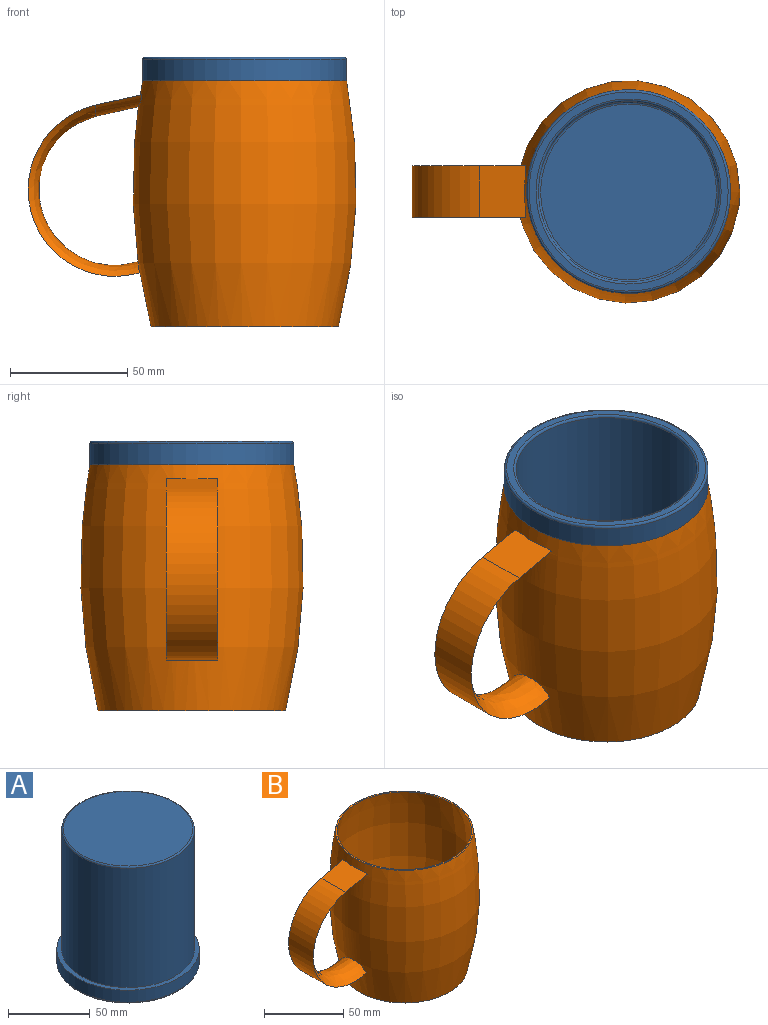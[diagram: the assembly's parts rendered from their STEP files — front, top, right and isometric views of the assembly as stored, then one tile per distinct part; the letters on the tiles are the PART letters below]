
ASSEMBLY  parts=2 mates=1
PART A: 11 faces, bbox 94.2x94.2x100 mm
  f0: cylinder r=38.5mm len=96mm, axis (0,0,-1), area 23222.7mm2, adj f7,f9
  f1: cylinder r=43.5mm len=87mm, axis (0,0,-1), area 2459.9mm2, adj f2,f10
  f2: plane 87x87mm, normal (0,0,1), area 791.7mm2, adj f1,f4
  f3: plane 85x85mm, normal (0,0,-1), area 772.8mm2, adj f9,f10
  f4: cylinder r=40.5mm len=89mm, axis (0,0,-1), area 22647.7mm2, adj f2,f8
  f5: plane 79x79mm, normal (0,0,1), area 4901.7mm2, adj f8
  f6: plane 75x75mm, normal (0,0,-1), area 4417.9mm2, adj f7
  f7: torus R=37.5mm, axis (0,0,1), area 376.4mm2, adj f0,f6
  f8: torus R=39.5mm, axis (0,0,1), area 396.1mm2, adj f4,f5
  f9: torus R=39.5mm, axis (0,0,1), area 383.6mm2, adj f0,f3
  f10: torus R=42.5mm, axis (0,0,1), area 425.7mm2, adj f1,f3
PART B: 14 faces, bbox 144.5x95.4x105.1 mm
  f0: revolved ~105x95.26mm, area 30252.5mm2, adj f1,f2,f7,f8,f9,f10,f11,f12
  f1: plane 87x87mm, normal (0,0,1), area 274.8mm2, adj f0,f4
  f2: plane 80x80mm, normal (0,0,-1), area 5026.5mm2, adj f0
  f3: plane 78.45x78.45mm, normal (0,0,1), area 4833.2mm2, adj f4
  f4: revolved ~104x93.27mm, area 29395mm2, adj f1,f3,f5,f6
  f5: bspline ~8x0.59mm, area 1.5mm2, adj f4,f6
  f6: plane 8.03x1.81mm, normal (1,0,0), area 9.6mm2, adj f4,f5
  f7: plane 4.16x2.1mm, normal (1,0,0), area 4.1mm2, adj f0,f10,f11
  f8: plane 4.16x2.1mm, normal (1,0,0), area 4.1mm2, adj f0,f10,f11
  f9: plane 22x4.47mm, normal (1,0,0.06), area 65.8mm2, adj f0,f12,f13
  f10: bspline ~22x19.51mm, area 475.2mm2, adj f0,f7,f8,f11,f12
  f11: plane 22x19.51mm, normal (-0.22,0,0.98), area 434.6mm2, adj f0,f7,f8,f10,f13
  f12: bspline ~77.85x51.77mm, area 2669.1mm2, adj f0,f9,f10,f13
  f13: cylinder r=37mm len=73.1mm, axis (0,-1,0), area 2608.7mm2, adj f9,f11,f12
PLACE A rot(axis=(1,0,0),180deg) t=(0,0,62.5)mm
PLACE B at identity fixed
MATE fastened A.f1 <-> B.f1  axis (0,0,-1) through (0,0,52.5)mm
